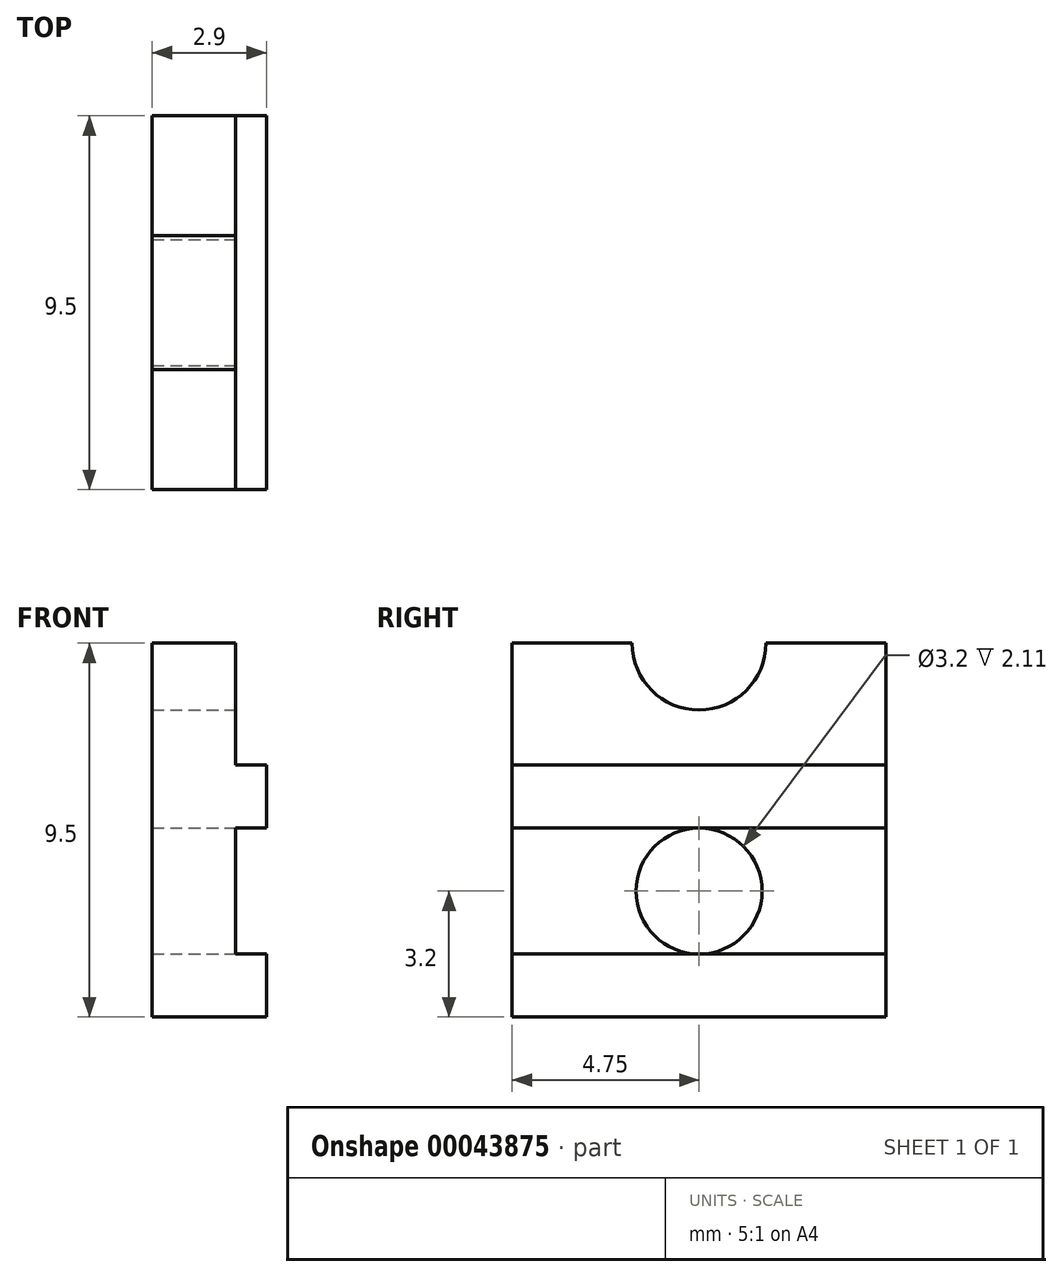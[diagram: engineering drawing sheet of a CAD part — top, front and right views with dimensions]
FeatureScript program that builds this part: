
annotation { "Feature Type Name" : "Feature", "Feature Type Description" : "" }
export const myFeature = defineFeature(function(context is Context, id is Id, definition is map)
    precondition{}
    {
        {
            var Q0;
            Q0=qCreatedBy(makeId("Front.planeOp"),FACE);
            var sketch = newSketch(context, id + "F0", { "sketchPlane" : qUnion([Q0])});
            skLineSegment(sketch, "E0.rect.bottom", {"start": v(1.45, -4.75) * mm, "end": v(-1.45, -4.75) * mm});
            skLineSegment(sketch, "E0.rect.top", {"start": v(0.66, 4.75) * mm, "end": v(-1.45, 4.75) * mm});
            skLineSegment(sketch, "E0.rect.left", {"start": v(1.45, -4.75) * mm, "end": v(1.45, -3.15) * mm});
            skLineSegment(sketch, "E0.rect.right", {"start": v(-1.45, -4.75) * mm, "end": v(-1.45, 4.75) * mm});
            skPoint(sketch, "E0.rect.middle", {"position": v(0, 0) * mm});
            skLineSegment(sketch, "E1", {"start": v(0.66, 4.75) * mm, "end": v(0.66, 1.65) * mm});
            skLineSegment(sketch, "E2", {"start": v(0.66, 1.65) * mm, "end": v(1.45, 1.65) * mm});
            skPoint(sketch, "E3.orphan", {"position": v(1.45, 4.75) * mm});
            skLineSegment(sketch, "E4", {"start": v(1.45, -3.15) * mm, "end": v(0.66, -3.15) * mm});
            skLineSegment(sketch, "E5", {"start": v(0.66, -3.15) * mm, "end": v(0.66, 0.05) * mm});
            skLineSegment(sketch, "E6", {"start": v(0.66, 0.05) * mm, "end": v(1.45, 0.05) * mm});
            skLineSegment(sketch, "E7.trimOffspring", {"start": v(1.45, 0.05) * mm, "end": v(1.45, 1.65) * mm});
            skSolve(sketch);
        }
        {
            var Q0;
            Q0 = qSketchRegion(id + "F0", true);
            extrude(context, id + "F1", {"entities" : qUnion([Q0]), "endBound" : BoundingType.SYMMETRIC, "depth" : 9.5 * mm});
        }
        {
            var Q0;
            Q0=makeQuery(id+"F1.opExtrude","SWEPT_FACE",FACE,{"disambiguationData":[OSD([sQuery(id+"F0.wireOp",EDGE,"E5")])]});
            var sketch = newSketch(context, id + "F2", { "sketchPlane" : qUnion([Q0])});
            skCircle(sketch, "E8", {"center": v(0, 4.75) * mm, "radius": 1.7 * mm});
            skSolve(sketch);
        }
        {
            var Q0;
            Q0 = qSketchRegion(id + "F2", true);
            extrude(context, id + "F3", {"entities" : qUnion([Q0]), "operationType" : NewBodyOperationType.REMOVE, "endBound" : BoundingType.THROUGH_ALL, "oppositeDirection" : true, "depth" : 25 * mm});
        }
        {
            var Q0;
            Q0=makeQuery(id+"F1.opExtrude","SWEPT_FACE",FACE,{"disambiguationData":[OSD([sQuery(id+"F0.wireOp",EDGE,"E5")])]});
            var sketch = newSketch(context, id + "F4", { "sketchPlane" : qUnion([Q0])});
            skCircle(sketch, "E9", {"center": v(0, -1.55) * mm, "radius": 1.6 * mm});
            skSolve(sketch);
        }
        {
            var Q0;
            Q0 = qSketchRegion(id + "F4", true);
            extrude(context, id + "F5", {"entities" : qUnion([Q0]), "operationType" : NewBodyOperationType.REMOVE, "endBound" : BoundingType.THROUGH_ALL, "oppositeDirection" : true, "depth" : 25 * mm});
        }
    });
